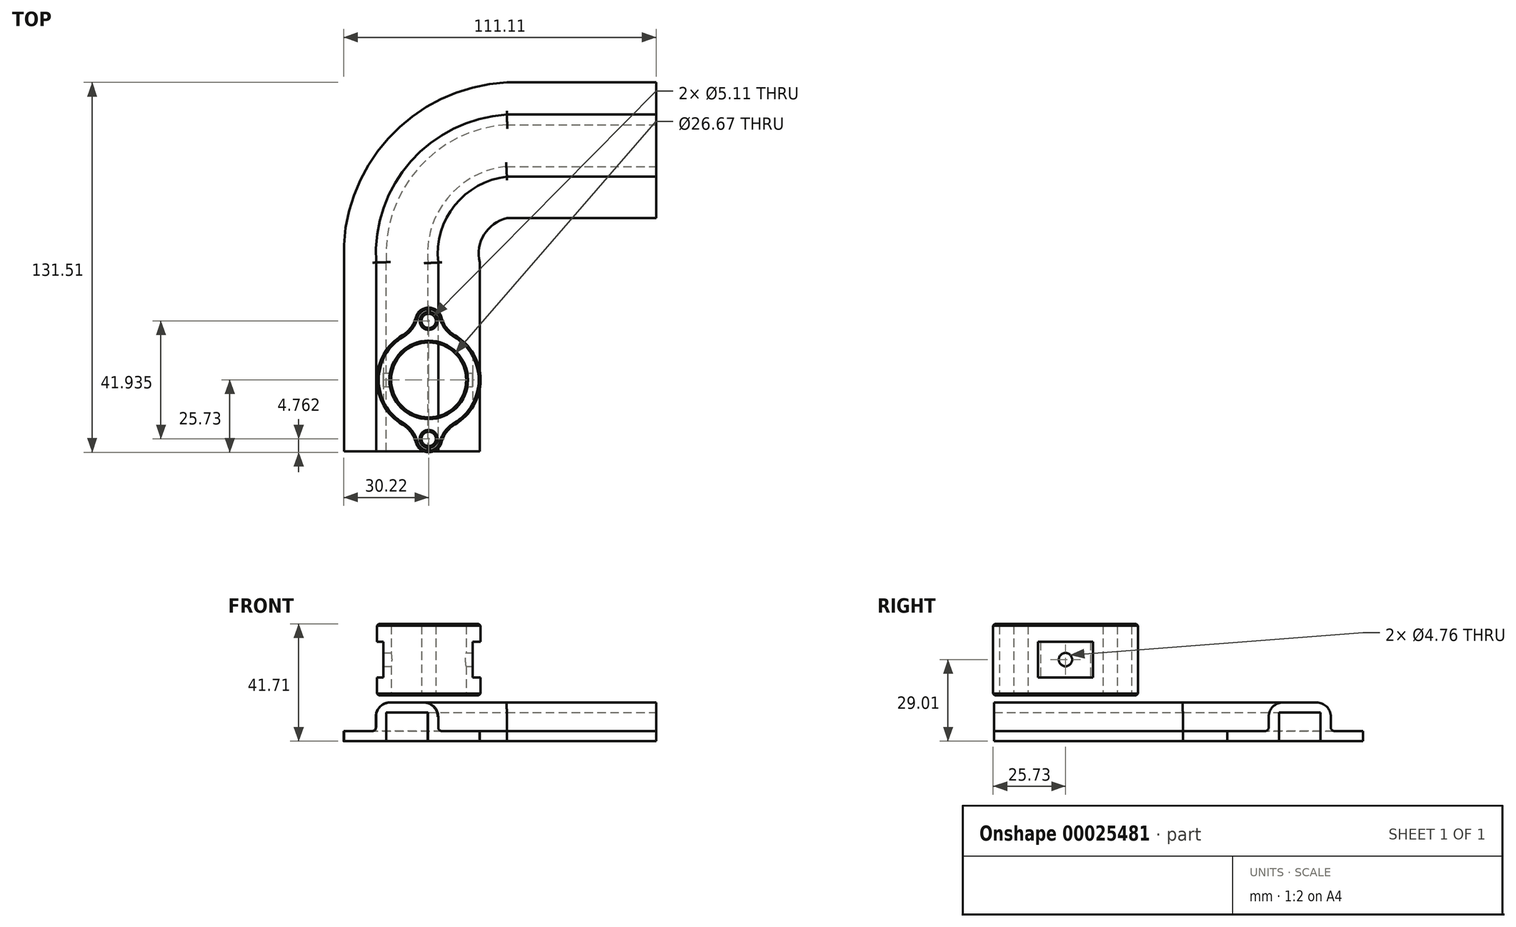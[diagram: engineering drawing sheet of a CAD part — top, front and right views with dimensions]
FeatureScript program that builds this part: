
annotation { "Feature Type Name" : "Feature", "Feature Type Description" : "" }
export const myFeature = defineFeature(function(context is Context, id is Id, definition is map)
    precondition{}
    {
        {
            var Q0;
            Q0=qCreatedBy(makeId("Top.planeOp"),FACE);
            var sketch = newSketch(context, id + "F0", { "sketchPlane" : qUnion([Q0])});
            skCircle(sketch, "E0", {"center": v(0, 0) * mm, "radius": 13.34 * mm});
            skCircle(sketch, "E1", {"center": v(0, 0) * mm, "radius": 18.41 * mm});
            skLineSegment(sketch, "E2.bottom", {"start": v(0, 18.41) * mm, "end": v(21.9, 18.41) * mm});
            skLineSegment(sketch, "E2.top", {"start": v(0, -18.41) * mm, "end": v(21.9, -18.41) * mm});
            skLineSegment(sketch, "E2.left", {"start": v(0, 18.41) * mm, "end": v(0, -18.42) * mm});
            skLineSegment(sketch, "E2.right", {"start": v(25.07, 15.24) * mm, "end": v(25.07, -15.24) * mm});
            skLineSegment(sketch, "E3", {"start": v(0, 0) * mm, "end": v(37.4, 0) * mm});
            skArc(sketch, "E4.0.startCap", {"start": v(0, -1.59) * mm, "mid": v(-1.59, 0) * mm, "end": v(0, 1.59) * mm});
            skArc(sketch, "E4.0.endCap", {"start": v(37.4, 1.59) * mm, "mid": v(39, 0) * mm, "end": v(37.4, -1.59) * mm});
            skLineSegment(sketch, "E4.0.left", {"start": v(0, 1.59) * mm, "end": v(37.4, 1.59) * mm});
            skLineSegment(sketch, "E4.0.right", {"start": v(0, -1.59) * mm, "end": v(37.4, -1.59) * mm});
            skPoint(sketch, "E5.visualSharp", {"position": v(25.07, 18.41) * mm});
            skArc(sketch, "E5.filletArc", {"start": v(25.07, 15.24) * mm, "mid": v(24.14, 17.49) * mm, "end": v(21.9, 18.41) * mm});
            skPoint(sketch, "E6.visualSharp", {"position": v(25.07, -18.41) * mm});
            skArc(sketch, "E6.filletArc", {"start": v(21.9, -18.42) * mm, "mid": v(24.14, -17.49) * mm, "end": v(25.07, -15.24) * mm});
            skCircle(sketch, "E7", {"center": v(0, 20.97) * mm, "radius": 2.55 * mm});
            skCircle(sketch, "E8", {"center": v(0, -20.97) * mm, "radius": 2.55 * mm});
            skCircle(sketch, "E9", {"center": v(0, 20.97) * mm, "radius": 4.76 * mm});
            skCircle(sketch, "E10", {"center": v(0, -20.97) * mm, "radius": 4.76 * mm});
            skCircle(sketch, "E11", {"center": v(-20.97, 0) * mm, "radius": 2.55 * mm});
            skCircle(sketch, "E12", {"center": v(-20.97, 0) * mm, "radius": 4.76 * mm});
            skPoint(sketch, "E13", {"position": v(25.07, 0) * mm});
            skSolve(sketch);
        }
        {
            var Q0;
            {var subQ5=sQuery(id+"F0.wireOp",EDGE,"E2.bottom");Q0=makeQuery(id+"F0.imprint","IMPRINT",FACE,{"disambiguationData":[TD([[makeQuery(id+"F0.imprint","IMPRINT",EDGE,{"derivedFrom":subQ5}),-1.0]])]});}
            var Q1;
            {var subQ5=sQuery(id+"F0.wireOp",EDGE,"E2.top");Q1=makeQuery(id+"F0.imprint","IMPRINT",FACE,{"disambiguationData":[TD([[makeQuery(id+"F0.imprint","IMPRINT",EDGE,{"derivedFrom":subQ5}),1.0]])]});}
            var Q2;
            {var subQ0=sQuery(id+"F0.wireOp",EDGE,"E2.left");var subQ1=sQuery(id+"F0.wireOp",EDGE,"E0");var subQ5=makeQuery(id+"F0.imprint","INTERSECT",VERTEX,{"disambiguationData":[OD(0.0)],"derivedFrom":[subQ1,subQ0]});Q2=makeQuery(id+"F0.imprint","IMPRINT",FACE,{"disambiguationData":[TD([[makeQuery(id+"F0.imprint","IMPRINT",EDGE,{"disambiguationData":[TD([[subQ5,-1.0]])],"derivedFrom":subQ1}),-1.0]])]});}
            var Q3;
            {var subQ0=sQuery(id+"F0.wireOp",EDGE,"E4.0.left");var subQ3=sQuery(id+"F0.wireOp",EDGE,"E0");var subQ4=makeQuery(id+"F0.imprint","INTERSECT",VERTEX,{"derivedFrom":[subQ3,subQ0]});Q3=makeQuery(id+"F0.imprint","IMPRINT",FACE,{"disambiguationData":[TD([[makeQuery(id+"F0.imprint","IMPRINT",EDGE,{"disambiguationData":[TD([[subQ4,-1.0]])],"derivedFrom":subQ3}),-1.0]])]});}
            var Q4;
            {var subQ3=sQuery(id+"F0.wireOp",EDGE,"E0");var subQ5=sQuery(id+"F0.wireOp",EDGE,"E2.left");var subQ6=makeQuery(id+"F0.imprint","INTERSECT",VERTEX,{"disambiguationData":[OD(1.0)],"derivedFrom":[subQ3,subQ5]});Q4=makeQuery(id+"F0.imprint","IMPRINT",FACE,{"disambiguationData":[TD([[makeQuery(id+"F0.imprint","IMPRINT",EDGE,{"disambiguationData":[TD([[subQ6,-1.0]])],"derivedFrom":subQ3}),-1.0]])]});}
            var Q5;
            {var subQ5=sQuery(id+"F0.wireOp",EDGE,"E7");Q5=makeQuery(id+"F0.imprint","IMPRINT",FACE,{"disambiguationData":[TD([[makeQuery(id+"F0.imprint","IMPRINT",EDGE,{"derivedFrom":subQ5}),-1.0]])]});}
            var Q6;
            {var subQ0=sQuery(id+"F0.wireOp",EDGE,"E9");var subQ3=sQuery(id+"F0.wireOp",EDGE,"E1");var subQ4=makeQuery(id+"F0.imprint","INTERSECT",VERTEX,{"disambiguationData":[OD(0.0)],"derivedFrom":[subQ3,subQ0]});Q6=makeQuery(id+"F0.imprint","IMPRINT",FACE,{"disambiguationData":[TD([[makeQuery(id+"F0.imprint","IMPRINT",EDGE,{"disambiguationData":[TD([[subQ4,-1.0]])],"derivedFrom":subQ0}),1.0]])]});}
            var Q7;
            {var subQ0=sQuery(id+"F0.wireOp",EDGE,"E9");var subQ3=sQuery(id+"F0.wireOp",EDGE,"E1");var subQ4=makeQuery(id+"F0.imprint","INTERSECT",VERTEX,{"disambiguationData":[OD(1.0)],"derivedFrom":[subQ3,subQ0]});Q7=makeQuery(id+"F0.imprint","IMPRINT",FACE,{"disambiguationData":[TD([[makeQuery(id+"F0.imprint","IMPRINT",EDGE,{"disambiguationData":[TD([[subQ4,1.0]])],"derivedFrom":subQ0}),1.0]])]});}
            var Q8;
            {var subQ5=sQuery(id+"F0.wireOp",EDGE,"E8");Q8=makeQuery(id+"F0.imprint","IMPRINT",FACE,{"disambiguationData":[TD([[makeQuery(id+"F0.imprint","IMPRINT",EDGE,{"derivedFrom":subQ5}),-1.0]])]});}
            var Q9;
            {var subQ0=sQuery(id+"F0.wireOp",EDGE,"E10");var subQ3=sQuery(id+"F0.wireOp",EDGE,"E1");var subQ4=makeQuery(id+"F0.imprint","INTERSECT",VERTEX,{"disambiguationData":[OD(0.0)],"derivedFrom":[subQ3,subQ0]});Q9=makeQuery(id+"F0.imprint","IMPRINT",FACE,{"disambiguationData":[TD([[makeQuery(id+"F0.imprint","IMPRINT",EDGE,{"disambiguationData":[TD([[subQ4,1.0]])],"derivedFrom":subQ0}),1.0]])]});}
            var Q10;
            {var subQ0=sQuery(id+"F0.wireOp",EDGE,"E10");var subQ3=sQuery(id+"F0.wireOp",EDGE,"E1");var subQ4=makeQuery(id+"F0.imprint","INTERSECT",VERTEX,{"disambiguationData":[OD(1.0)],"derivedFrom":[subQ3,subQ0]});Q10=makeQuery(id+"F0.imprint","IMPRINT",FACE,{"disambiguationData":[TD([[makeQuery(id+"F0.imprint","IMPRINT",EDGE,{"disambiguationData":[TD([[subQ4,-1.0]])],"derivedFrom":subQ0}),1.0]])]});}
            var Q11;
            {var subQ0=sQuery(id+"F0.wireOp",EDGE,"E12");var subQ1=sQuery(id+"F0.wireOp",EDGE,"E1");var subQ3=makeQuery(id+"F0.imprint","INTERSECT",VERTEX,{"disambiguationData":[OD(0.0)],"derivedFrom":[subQ1,subQ0]});Q11=makeQuery(id+"F0.imprint","IMPRINT",FACE,{"disambiguationData":[TD([[makeQuery(id+"F0.imprint","IMPRINT",EDGE,{"disambiguationData":[TD([[subQ3,-1.0]])],"derivedFrom":subQ1}),1.0]])]});}
            var Q12;
            {var subQ3=sQuery(id+"F0.wireOp",EDGE,"E0");var subQ5=sQuery(id+"F0.wireOp",EDGE,"E4.0.left");var subQ7=makeQuery(id+"F0.imprint","INTERSECT",VERTEX,{"derivedFrom":[subQ3,subQ5]});Q12=makeQuery(id+"F0.imprint","IMPRINT",FACE,{"disambiguationData":[TD([[makeQuery(id+"F0.imprint","IMPRINT",EDGE,{"disambiguationData":[TD([[subQ7,1.0]])],"derivedFrom":subQ3}),-1.0]])]});}
            var Q13;
            {var subQ3=sQuery(id+"F0.wireOp",EDGE,"E0");var subQ5=sQuery(id+"F0.wireOp",EDGE,"E3");var subQ7=makeQuery(id+"F0.imprint","INTERSECT",VERTEX,{"derivedFrom":[subQ3,subQ5]});Q13=makeQuery(id+"F0.imprint","IMPRINT",FACE,{"disambiguationData":[TD([[makeQuery(id+"F0.imprint","IMPRINT",EDGE,{"disambiguationData":[TD([[subQ7,1.0]])],"derivedFrom":subQ3}),-1.0]])]});}
            extrude(context, id + "F1", {"entities" : qUnion([Q0, Q1, Q2, Q3, Q4, Q5, Q6, Q7, Q8, Q9, Q10, Q11, Q12, Q13]), "depth" : 25.4 * mm});
        }
        {
            var Q0;
            Q0=makeQuery(id+"F1.opExtrude","SWEPT_EDGE",EDGE,{"disambiguationData":[OSD([sQuery(id+"F0.wireOp",EDGE,"E2.bottom"),sQuery(id+"F0.wireOp",EDGE,"E9")])]});
            var Q1;
            Q1=makeQuery(id+"F1.opExtrude","SWEPT_EDGE",EDGE,{"disambiguationData":[OSD([sQuery(id+"F0.wireOp",EDGE,"E1"),sQuery(id+"F0.wireOp",EDGE,"E9")])]});
            var Q2;
            Q2=makeQuery(id+"F1.opExtrude","SWEPT_EDGE",EDGE,{"disambiguationData":[OSD([sQuery(id+"F0.wireOp",EDGE,"E2.top"),sQuery(id+"F0.wireOp",EDGE,"E10")])]});
            var Q3;
            Q3=makeQuery(id+"F1.opExtrude","SWEPT_EDGE",EDGE,{"disambiguationData":[OSD([sQuery(id+"F0.wireOp",EDGE,"E1"),sQuery(id+"F0.wireOp",EDGE,"E10")])]});
            var Q4;
            {var subQ0=sQuery(id+"F0.wireOp",EDGE,"E1");var subQ1=sQuery(id+"F0.wireOp",EDGE,"E12");Q4=makeQuery(id+"F1.opExtrude","SWEPT_EDGE",EDGE,{"disambiguationData":[OSD([subQ0,subQ1]),TDD([makeQuery(id+"F0.imprint","INTERSECT",VERTEX,{"disambiguationData":[OD(1.0)],"derivedFrom":[subQ0,subQ1]})])]});}
            var Q5;
            {var subQ0=sQuery(id+"F0.wireOp",EDGE,"E1");var subQ1=sQuery(id+"F0.wireOp",EDGE,"E12");Q5=makeQuery(id+"F1.opExtrude","SWEPT_EDGE",EDGE,{"disambiguationData":[OSD([subQ0,subQ1]),TDD([makeQuery(id+"F0.imprint","INTERSECT",VERTEX,{"disambiguationData":[OD(0.0)],"derivedFrom":[subQ0,subQ1]})])]});}
            fillet(context, id + "F2", {"entities" : qUnion([Q0, Q1, Q2, Q3, Q4, Q5]), "radius" : 10.16 * mm, "tangentPropagation" : true, "allowEdgeOverflow" : false});
        }
        {
            var Q0;
            {var subQ0=sQuery(id+"F0.wireOp",EDGE,"E2.right");Q0=makeQuery(id+"F1.opExtrude","CAP_EDGE",EDGE,{"disambiguationData":[OSD([subQ0]),TDD([makeQuery(id+"F0.imprint","IMPRINT",EDGE,{"disambiguationData":[TD([[makeQuery(id+"F0.imprint","INTERSECT",VERTEX,{"derivedFrom":[subQ0,sQuery(id+"F0.wireOp",EDGE,"E6.filletArc")]}),1.0]])],"derivedFrom":subQ0})])],"isStart":false});}
            var Q1;
            Q1=makeQuery(id+"F1.opExtrude","CAP_EDGE",EDGE,{"disambiguationData":[OSD([sQuery(id+"F0.wireOp",EDGE,"E6.filletArc")])],"isStart":false});
            var Q2;
            Q2=makeQuery(id+"F1.opExtrude","CAP_EDGE",EDGE,{"disambiguationData":[OSD([sQuery(id+"F0.wireOp",EDGE,"E2.top")])],"isStart":false});
            var Q3;
            {var subQ0=sQuery(id+"F0.wireOp",EDGE,"E2.top");var subQ1=sQuery(id+"F0.wireOp",EDGE,"E10");Q3=makeQuery(id+"F2.opFillet","BLEND_EDGE",EDGE,{"blendedFrom":[makeQuery(id+"F1.opExtrude","SWEPT_EDGE",EDGE,{"disambiguationData":[OSD([subQ0,subQ1])]}),makeQuery(id+"F1.opExtrude","CAP_FACE",FACE,{"disambiguationData":[OSD([sQuery(id+"F0.wireOp",EDGE,"E0"),sQuery(id+"F0.wireOp",EDGE,"E1"),sQuery(id+"F0.wireOp",EDGE,"E2.bottom"),subQ0,sQuery(id+"F0.wireOp",EDGE,"E2.right"),sQuery(id+"F0.wireOp",EDGE,"E4.0.left"),sQuery(id+"F0.wireOp",EDGE,"E4.0.right"),sQuery(id+"F0.wireOp",EDGE,"E5.filletArc"),sQuery(id+"F0.wireOp",EDGE,"E6.filletArc"),sQuery(id+"F0.wireOp",EDGE,"E7"),sQuery(id+"F0.wireOp",EDGE,"E8"),sQuery(id+"F0.wireOp",EDGE,"E9"),subQ1])],"isStart":false})],"blendedInto":[makeQuery(id+"F1.opExtrude","CAP_FACE",FACE,{"disambiguationData":[OSD([sQuery(id+"F0.wireOp",EDGE,"E0"),sQuery(id+"F0.wireOp",EDGE,"E1"),sQuery(id+"F0.wireOp",EDGE,"E2.bottom"),subQ0,sQuery(id+"F0.wireOp",EDGE,"E2.right"),sQuery(id+"F0.wireOp",EDGE,"E4.0.left"),sQuery(id+"F0.wireOp",EDGE,"E4.0.right"),sQuery(id+"F0.wireOp",EDGE,"E5.filletArc"),sQuery(id+"F0.wireOp",EDGE,"E6.filletArc"),sQuery(id+"F0.wireOp",EDGE,"E7"),sQuery(id+"F0.wireOp",EDGE,"E8"),sQuery(id+"F0.wireOp",EDGE,"E9"),subQ1])],"isStart":false})]});}
            var Q4;
            Q4=makeQuery(id+"F1.opExtrude","CAP_EDGE",EDGE,{"disambiguationData":[OSD([sQuery(id+"F0.wireOp",EDGE,"E10")])],"isStart":false});
            var Q5;
            {var subQ0=sQuery(id+"F0.wireOp",EDGE,"E1");var subQ1=sQuery(id+"F0.wireOp",EDGE,"E10");Q5=makeQuery(id+"F2.opFillet","BLEND_EDGE",EDGE,{"blendedFrom":[makeQuery(id+"F1.opExtrude","SWEPT_EDGE",EDGE,{"disambiguationData":[OSD([subQ0,subQ1])]}),makeQuery(id+"F1.opExtrude","CAP_FACE",FACE,{"disambiguationData":[OSD([sQuery(id+"F0.wireOp",EDGE,"E0"),subQ0,sQuery(id+"F0.wireOp",EDGE,"E2.bottom"),sQuery(id+"F0.wireOp",EDGE,"E2.top"),sQuery(id+"F0.wireOp",EDGE,"E2.right"),sQuery(id+"F0.wireOp",EDGE,"E4.0.left"),sQuery(id+"F0.wireOp",EDGE,"E4.0.right"),sQuery(id+"F0.wireOp",EDGE,"E5.filletArc"),sQuery(id+"F0.wireOp",EDGE,"E6.filletArc"),sQuery(id+"F0.wireOp",EDGE,"E7"),sQuery(id+"F0.wireOp",EDGE,"E8"),sQuery(id+"F0.wireOp",EDGE,"E9"),subQ1])],"isStart":false})],"blendedInto":[makeQuery(id+"F1.opExtrude","CAP_FACE",FACE,{"disambiguationData":[OSD([sQuery(id+"F0.wireOp",EDGE,"E0"),subQ0,sQuery(id+"F0.wireOp",EDGE,"E2.bottom"),sQuery(id+"F0.wireOp",EDGE,"E2.top"),sQuery(id+"F0.wireOp",EDGE,"E2.right"),sQuery(id+"F0.wireOp",EDGE,"E4.0.left"),sQuery(id+"F0.wireOp",EDGE,"E4.0.right"),sQuery(id+"F0.wireOp",EDGE,"E5.filletArc"),sQuery(id+"F0.wireOp",EDGE,"E6.filletArc"),sQuery(id+"F0.wireOp",EDGE,"E7"),sQuery(id+"F0.wireOp",EDGE,"E8"),sQuery(id+"F0.wireOp",EDGE,"E9"),subQ1])],"isStart":false})]});}
            var Q6;
            Q6=makeQuery(id+"F1.opExtrude","CAP_EDGE",EDGE,{"disambiguationData":[OSD([sQuery(id+"F0.wireOp",EDGE,"E1")])],"isStart":false});
            var Q7;
            {var subQ0=sQuery(id+"F0.wireOp",EDGE,"E1");var subQ1=sQuery(id+"F0.wireOp",EDGE,"E9");Q7=makeQuery(id+"F2.opFillet","BLEND_EDGE",EDGE,{"blendedFrom":[makeQuery(id+"F1.opExtrude","SWEPT_EDGE",EDGE,{"disambiguationData":[OSD([subQ0,subQ1])]}),makeQuery(id+"F1.opExtrude","CAP_FACE",FACE,{"disambiguationData":[OSD([sQuery(id+"F0.wireOp",EDGE,"E0"),subQ0,sQuery(id+"F0.wireOp",EDGE,"E2.bottom"),sQuery(id+"F0.wireOp",EDGE,"E2.top"),sQuery(id+"F0.wireOp",EDGE,"E2.right"),sQuery(id+"F0.wireOp",EDGE,"E4.0.left"),sQuery(id+"F0.wireOp",EDGE,"E4.0.right"),sQuery(id+"F0.wireOp",EDGE,"E5.filletArc"),sQuery(id+"F0.wireOp",EDGE,"E6.filletArc"),sQuery(id+"F0.wireOp",EDGE,"E7"),sQuery(id+"F0.wireOp",EDGE,"E8"),subQ1,sQuery(id+"F0.wireOp",EDGE,"E10")])],"isStart":false})],"blendedInto":[makeQuery(id+"F1.opExtrude","CAP_FACE",FACE,{"disambiguationData":[OSD([sQuery(id+"F0.wireOp",EDGE,"E0"),subQ0,sQuery(id+"F0.wireOp",EDGE,"E2.bottom"),sQuery(id+"F0.wireOp",EDGE,"E2.top"),sQuery(id+"F0.wireOp",EDGE,"E2.right"),sQuery(id+"F0.wireOp",EDGE,"E4.0.left"),sQuery(id+"F0.wireOp",EDGE,"E4.0.right"),sQuery(id+"F0.wireOp",EDGE,"E5.filletArc"),sQuery(id+"F0.wireOp",EDGE,"E6.filletArc"),sQuery(id+"F0.wireOp",EDGE,"E7"),sQuery(id+"F0.wireOp",EDGE,"E8"),subQ1,sQuery(id+"F0.wireOp",EDGE,"E10")])],"isStart":false})]});}
            var Q8;
            Q8=makeQuery(id+"F1.opExtrude","CAP_EDGE",EDGE,{"disambiguationData":[OSD([sQuery(id+"F0.wireOp",EDGE,"E9")])],"isStart":false});
            var Q9;
            {var subQ0=sQuery(id+"F0.wireOp",EDGE,"E2.bottom");var subQ1=sQuery(id+"F0.wireOp",EDGE,"E9");Q9=makeQuery(id+"F2.opFillet","BLEND_EDGE",EDGE,{"blendedFrom":[makeQuery(id+"F1.opExtrude","SWEPT_EDGE",EDGE,{"disambiguationData":[OSD([subQ0,subQ1])]}),makeQuery(id+"F1.opExtrude","CAP_FACE",FACE,{"disambiguationData":[OSD([sQuery(id+"F0.wireOp",EDGE,"E0"),sQuery(id+"F0.wireOp",EDGE,"E1"),subQ0,sQuery(id+"F0.wireOp",EDGE,"E2.top"),sQuery(id+"F0.wireOp",EDGE,"E2.right"),sQuery(id+"F0.wireOp",EDGE,"E4.0.left"),sQuery(id+"F0.wireOp",EDGE,"E4.0.right"),sQuery(id+"F0.wireOp",EDGE,"E5.filletArc"),sQuery(id+"F0.wireOp",EDGE,"E6.filletArc"),sQuery(id+"F0.wireOp",EDGE,"E7"),sQuery(id+"F0.wireOp",EDGE,"E8"),subQ1,sQuery(id+"F0.wireOp",EDGE,"E10")])],"isStart":false})],"blendedInto":[makeQuery(id+"F1.opExtrude","CAP_FACE",FACE,{"disambiguationData":[OSD([sQuery(id+"F0.wireOp",EDGE,"E0"),sQuery(id+"F0.wireOp",EDGE,"E1"),subQ0,sQuery(id+"F0.wireOp",EDGE,"E2.top"),sQuery(id+"F0.wireOp",EDGE,"E2.right"),sQuery(id+"F0.wireOp",EDGE,"E4.0.left"),sQuery(id+"F0.wireOp",EDGE,"E4.0.right"),sQuery(id+"F0.wireOp",EDGE,"E5.filletArc"),sQuery(id+"F0.wireOp",EDGE,"E6.filletArc"),sQuery(id+"F0.wireOp",EDGE,"E7"),sQuery(id+"F0.wireOp",EDGE,"E8"),subQ1,sQuery(id+"F0.wireOp",EDGE,"E10")])],"isStart":false})]});}
            var Q10;
            Q10=makeQuery(id+"F1.opExtrude","CAP_EDGE",EDGE,{"disambiguationData":[OSD([sQuery(id+"F0.wireOp",EDGE,"E2.bottom")])],"isStart":false});
            var Q11;
            Q11=makeQuery(id+"F1.opExtrude","CAP_EDGE",EDGE,{"disambiguationData":[OSD([sQuery(id+"F0.wireOp",EDGE,"E5.filletArc")])],"isStart":false});
            var Q12;
            {var subQ0=sQuery(id+"F0.wireOp",EDGE,"E2.right");Q12=makeQuery(id+"F1.opExtrude","CAP_EDGE",EDGE,{"disambiguationData":[OSD([subQ0]),TDD([makeQuery(id+"F0.imprint","IMPRINT",EDGE,{"disambiguationData":[TD([[makeQuery(id+"F0.imprint","INTERSECT",VERTEX,{"derivedFrom":[subQ0,sQuery(id+"F0.wireOp",EDGE,"E5.filletArc")]}),-1.0]])],"derivedFrom":subQ0})])],"isStart":false});}
            var Q13;
            Q13=makeQuery(id+"F1.opExtrude","CAP_EDGE",EDGE,{"disambiguationData":[OSD([sQuery(id+"F0.wireOp",EDGE,"E0")])],"isStart":false});
            var Q14;
            {var subQ0=sQuery(id+"F0.wireOp",EDGE,"E2.right");Q14=makeQuery(id+"F1.opExtrude","CAP_EDGE",EDGE,{"disambiguationData":[OSD([subQ0]),TDD([makeQuery(id+"F0.imprint","IMPRINT",EDGE,{"disambiguationData":[TD([[makeQuery(id+"F0.imprint","INTERSECT",VERTEX,{"derivedFrom":[subQ0,sQuery(id+"F0.wireOp",EDGE,"E6.filletArc")]}),1.0]])],"derivedFrom":subQ0})])],"isStart":true});}
            var Q15;
            Q15=makeQuery(id+"F1.opExtrude","CAP_EDGE",EDGE,{"disambiguationData":[OSD([sQuery(id+"F0.wireOp",EDGE,"E6.filletArc")])],"isStart":true});
            var Q16;
            {var subQ0=sQuery(id+"F0.wireOp",EDGE,"E1");var subQ1=sQuery(id+"F0.wireOp",EDGE,"E10");Q16=makeQuery(id+"F2.opFillet","BLEND_EDGE",EDGE,{"blendedFrom":[makeQuery(id+"F1.opExtrude","SWEPT_EDGE",EDGE,{"disambiguationData":[OSD([subQ0,subQ1]),TDD([makeQuery(id+"F0.imprint","INTERSECT",VERTEX,{"disambiguationData":[OD(1.0)],"derivedFrom":[subQ0,subQ1]})])]}),makeQuery(id+"F1.opExtrude","CAP_FACE",FACE,{"disambiguationData":[OSD([sQuery(id+"F0.wireOp",EDGE,"E0"),subQ0,sQuery(id+"F0.wireOp",EDGE,"E7"),sQuery(id+"F0.wireOp",EDGE,"E8"),sQuery(id+"F0.wireOp",EDGE,"E9"),subQ1])],"isStart":true})],"blendedInto":[makeQuery(id+"F1.opExtrude","CAP_FACE",FACE,{"disambiguationData":[OSD([sQuery(id+"F0.wireOp",EDGE,"E0"),subQ0,sQuery(id+"F0.wireOp",EDGE,"E7"),sQuery(id+"F0.wireOp",EDGE,"E8"),sQuery(id+"F0.wireOp",EDGE,"E9"),subQ1])],"isStart":true})]});}
            var Q17;
            Q17=makeQuery(id+"F1.opExtrude","CAP_EDGE",EDGE,{"disambiguationData":[OSD([sQuery(id+"F0.wireOp",EDGE,"E0")])],"isStart":true});
            var Q18;
            Q18=makeQuery(id+"F1.opExtrude","CAP_EDGE",EDGE,{"disambiguationData":[OSD([sQuery(id+"F0.wireOp",EDGE,"E8")])],"isStart":false});
            var Q19;
            Q19=makeQuery(id+"F1.opExtrude","CAP_EDGE",EDGE,{"disambiguationData":[OSD([sQuery(id+"F0.wireOp",EDGE,"E7")])],"isStart":false});
            var Q20;
            Q20=makeQuery(id+"F1.opExtrude","CAP_EDGE",EDGE,{"disambiguationData":[OSD([sQuery(id+"F0.wireOp",EDGE,"E8")])],"isStart":true});
            var Q21;
            Q21=makeQuery(id+"F1.opExtrude","CAP_EDGE",EDGE,{"disambiguationData":[OSD([sQuery(id+"F0.wireOp",EDGE,"E7")])],"isStart":true});
            chamfer(context, id + "F3", {"entities" : qUnion([Q0, Q1, Q2, Q3, Q4, Q5, Q6, Q7, Q8, Q9, Q10, Q11, Q12, Q13, Q14, Q15, Q16, Q17, Q18, Q19, Q20, Q21]), "width" : 0.64 * mm, "tangentPropagation" : true});
        }
        {
            var Q0;
            Q0=qCreatedBy(makeId("Front.planeOp"),FACE);
            var sketch = newSketch(context, id + "F4", { "sketchPlane" : qUnion([Q0])});
            skLineSegment(sketch, "E14", {"start": v(-30.14, -12.68) * mm, "end": v(-18.71, -12.68) * mm});
            skLineSegment(sketch, "E15", {"start": v(-18.71, -12.68) * mm, "end": v(-18.71, -2.52) * mm});
            skLineSegment(sketch, "E16", {"start": v(-18.71, -2.52) * mm, "end": v(3.39, -2.52) * mm});
            skLineSegment(sketch, "E17", {"start": v(3.39, -2.52) * mm, "end": v(3.39, -12.68) * mm});
            skLineSegment(sketch, "E18", {"start": v(3.39, -12.68) * mm, "end": v(18.12, -12.68) * mm});
            skLineSegment(sketch, "E19.0", {"start": v(-0.25, -16.3) * mm, "end": v(18.12, -16.3) * mm});
            skLineSegment(sketch, "E19.1", {"start": v(-30.14, -16.3) * mm, "end": v(-15.08, -16.3) * mm});
            skLineSegment(sketch, "E19.2", {"start": v(-15.08, -16.3) * mm, "end": v(-15.08, -6.15) * mm});
            skLineSegment(sketch, "E19.3", {"start": v(-15.08, -6.15) * mm, "end": v(-0.25, -6.15) * mm});
            skLineSegment(sketch, "E19.4", {"start": v(-0.25, -6.15) * mm, "end": v(-0.25, -16.3) * mm});
            skLineSegment(sketch, "E20", {"start": v(-30.14, -16.3) * mm, "end": v(-30.14, -12.68) * mm});
            skLineSegment(sketch, "E21", {"start": v(18.12, -16.3) * mm, "end": v(18.12, -12.68) * mm});
            skSolve(sketch);
        }
        {
            var Q0;
            Q0 = qSketchRegion(id + "F4", true);
            extrude(context, id + "F5", {"entities" : qUnion([Q0]), "depth" : 25.4 * mm});
        }
        {
            var Q0;
            Q0=qCreatedBy(makeId("Top.planeOp"),FACE);
            var sketch = newSketch(context, id + "F6", { "sketchPlane" : qUnion([Q0])});
            skLineSegment(sketch, "E22", {"start": v(-7.25, 3.05) * mm, "end": v(-7.25, 44.79) * mm});
            skLineSegment(sketch, "E23", {"start": v(30.85, 82.89) * mm, "end": v(83.94, 82.89) * mm});
            skPoint(sketch, "E24.visualSharp", {"position": v(-7.25, 82.89) * mm});
            skArc(sketch, "E24.filletArc", {"start": v(30.85, 82.89) * mm, "mid": v(3.91, 71.73) * mm, "end": v(-7.25, 44.79) * mm});
            skSolve(sketch);
        }
        {
            var Q0;
            Q0=makeQuery(id+"F5.opExtrude","CAP_FACE",FACE,{"disambiguationData":[OSD([sQuery(id+"F4.wireOp",EDGE,"E14"),sQuery(id+"F4.wireOp",EDGE,"E15"),sQuery(id+"F4.wireOp",EDGE,"E16"),sQuery(id+"F4.wireOp",EDGE,"E17"),sQuery(id+"F4.wireOp",EDGE,"E18"),sQuery(id+"F4.wireOp",EDGE,"E19.0"),sQuery(id+"F4.wireOp",EDGE,"E19.1"),sQuery(id+"F4.wireOp",EDGE,"E19.2"),sQuery(id+"F4.wireOp",EDGE,"E19.3"),sQuery(id+"F4.wireOp",EDGE,"E19.4"),sQuery(id+"F4.wireOp",EDGE,"E20"),sQuery(id+"F4.wireOp",EDGE,"E21")])],"isStart":true});
            var Q1;
            Q1=sQuery(id+"F6.wireOp",EDGE,"E22");
            var Q2;
            Q2=sQuery(id+"F6.wireOp",EDGE,"E24.filletArc");
            var Q3;
            Q3=sQuery(id+"F6.wireOp",EDGE,"E23");
            sweep(context, id + "F7", {"operationType" : NewBodyOperationType.ADD, "profiles" : qUnion([Q0]), "path" : qUnion([Q1, Q2, Q3])});
        }
        {
            var Q0;
            Q0=makeQuery(id+"F7.opSweep","SWEPT_EDGE",EDGE,{"disambiguationData":[OSD([sQuery(id+"F4.wireOp",EDGE,"E16"),sQuery(id+"F4.wireOp",EDGE,"E17"),sQuery(id+"F6.wireOp",EDGE,"E23")])]});
            var Q1;
            Q1=makeQuery(id+"F7.opSweep","SWEPT_EDGE",EDGE,{"disambiguationData":[OSD([sQuery(id+"F4.wireOp",EDGE,"E16"),sQuery(id+"F4.wireOp",EDGE,"E17"),sQuery(id+"F6.wireOp",EDGE,"E24.filletArc")])]});
            var Q2;
            {var subQ0=sQuery(id+"F4.wireOp",EDGE,"E16");var subQ1=sQuery(id+"F4.wireOp",EDGE,"E17");Q2=makeQuery(id+"F7.boolean.opBoolean","MERGE",EDGE,{"derivedFrom":[makeQuery(id+"F5.opExtrude","SWEPT_EDGE",EDGE,{"disambiguationData":[OSD([subQ0,subQ1])]}),makeQuery(id+"F7.opSweep","SWEPT_EDGE",EDGE,{"disambiguationData":[OSD([subQ0,subQ1,sQuery(id+"F6.wireOp",EDGE,"E22")])]})]});}
            var Q3;
            {var subQ0=sQuery(id+"F4.wireOp",EDGE,"E15");var subQ1=sQuery(id+"F4.wireOp",EDGE,"E16");Q3=makeQuery(id+"F7.boolean.opBoolean","MERGE",EDGE,{"derivedFrom":[makeQuery(id+"F5.opExtrude","SWEPT_EDGE",EDGE,{"disambiguationData":[OSD([subQ0,subQ1])]}),makeQuery(id+"F7.opSweep","SWEPT_EDGE",EDGE,{"disambiguationData":[OSD([subQ0,subQ1,sQuery(id+"F6.wireOp",EDGE,"E22")])]})]});}
            var Q4;
            Q4=makeQuery(id+"F7.opSweep","SWEPT_EDGE",EDGE,{"disambiguationData":[OSD([sQuery(id+"F4.wireOp",EDGE,"E15"),sQuery(id+"F4.wireOp",EDGE,"E16"),sQuery(id+"F6.wireOp",EDGE,"E24.filletArc")])]});
            var Q5;
            Q5=makeQuery(id+"F7.opSweep","SWEPT_EDGE",EDGE,{"disambiguationData":[OSD([sQuery(id+"F4.wireOp",EDGE,"E15"),sQuery(id+"F4.wireOp",EDGE,"E16"),sQuery(id+"F6.wireOp",EDGE,"E23")])]});
            fillet(context, id + "F8", {"entities" : qUnion([Q0, Q1, Q2, Q3, Q4, Q5]), "radius" : 5.08 * mm, "tangentPropagation" : true, "allowEdgeOverflow" : false});
        }
        {
            var Q0;
            Q0=makeQuery(id+"F7.opSweep","SWEPT_EDGE",EDGE,{"disambiguationData":[OSD([sQuery(id+"F4.wireOp",EDGE,"E14"),sQuery(id+"F4.wireOp",EDGE,"E15"),sQuery(id+"F6.wireOp",EDGE,"E23")])]});
            var Q1;
            Q1=makeQuery(id+"F7.opSweep","SWEPT_EDGE",EDGE,{"disambiguationData":[OSD([sQuery(id+"F4.wireOp",EDGE,"E14"),sQuery(id+"F4.wireOp",EDGE,"E15"),sQuery(id+"F6.wireOp",EDGE,"E24.filletArc")])]});
            var Q2;
            {var subQ0=sQuery(id+"F4.wireOp",EDGE,"E14");var subQ1=sQuery(id+"F4.wireOp",EDGE,"E15");Q2=makeQuery(id+"F7.boolean.opBoolean","MERGE",EDGE,{"derivedFrom":[makeQuery(id+"F5.opExtrude","SWEPT_EDGE",EDGE,{"disambiguationData":[OSD([subQ0,subQ1])]}),makeQuery(id+"F7.opSweep","SWEPT_EDGE",EDGE,{"disambiguationData":[OSD([subQ0,subQ1,sQuery(id+"F6.wireOp",EDGE,"E22")])]})]});}
            var Q3;
            {var subQ0=sQuery(id+"F4.wireOp",EDGE,"E17");var subQ1=sQuery(id+"F4.wireOp",EDGE,"E18");Q3=makeQuery(id+"F7.boolean.opBoolean","MERGE",EDGE,{"derivedFrom":[makeQuery(id+"F5.opExtrude","SWEPT_EDGE",EDGE,{"disambiguationData":[OSD([subQ0,subQ1])]}),makeQuery(id+"F7.opSweep","SWEPT_EDGE",EDGE,{"disambiguationData":[OSD([subQ0,subQ1,sQuery(id+"F6.wireOp",EDGE,"E22")])]})]});}
            var Q4;
            Q4=makeQuery(id+"F7.opSweep","SWEPT_EDGE",EDGE,{"disambiguationData":[OSD([sQuery(id+"F4.wireOp",EDGE,"E17"),sQuery(id+"F4.wireOp",EDGE,"E18"),sQuery(id+"F6.wireOp",EDGE,"E24.filletArc")])]});
            var Q5;
            Q5=makeQuery(id+"F7.opSweep","SWEPT_EDGE",EDGE,{"disambiguationData":[OSD([sQuery(id+"F4.wireOp",EDGE,"E17"),sQuery(id+"F4.wireOp",EDGE,"E18"),sQuery(id+"F6.wireOp",EDGE,"E23")])]});
            fillet(context, id + "F9", {"entities" : qUnion([Q0, Q1, Q2, Q3, Q4, Q5]), "radius" : 1.27 * mm, "tangentPropagation" : true, "allowEdgeOverflow" : false});
        }
        {
            var Q0;
            Q0=qCreatedBy(makeId("Front.planeOp"),FACE);
            var sketch = newSketch(context, id + "F10", { "sketchPlane" : qUnion([Q0])});
            skLineSegment(sketch, "E25", {"start": v(-22.48, 12.7) * mm, "end": v(21.97, 12.7) * mm, "construction": true});
            skLineSegment(sketch, "E26.rect.bottom", {"start": v(-16.13, 6.35) * mm, "end": v(-28.83, 6.35) * mm});
            skLineSegment(sketch, "E26.rect.top", {"start": v(-16.13, 19.05) * mm, "end": v(-28.83, 19.05) * mm});
            skLineSegment(sketch, "E26.rect.left", {"start": v(-16.13, 6.35) * mm, "end": v(-16.13, 19.05) * mm});
            skLineSegment(sketch, "E26.rect.right", {"start": v(-28.83, 6.35) * mm, "end": v(-28.83, 19.05) * mm});
            skPoint(sketch, "E26.rect.middle", {"position": v(-22.48, 12.7) * mm});
            skLineSegment(sketch, "E27.rect.bottom", {"start": v(15.62, 6.35) * mm, "end": v(28.32, 6.35) * mm});
            skLineSegment(sketch, "E27.rect.top", {"start": v(15.62, 19.05) * mm, "end": v(28.32, 19.05) * mm});
            skLineSegment(sketch, "E27.rect.left", {"start": v(15.62, 6.35) * mm, "end": v(15.62, 19.05) * mm});
            skLineSegment(sketch, "E27.rect.right", {"start": v(28.32, 6.35) * mm, "end": v(28.32, 19.05) * mm});
            skPoint(sketch, "E27.rect.middle", {"position": v(21.97, 12.7) * mm});
            skLineSegment(sketch, "E28", {"start": v(-0.25, -8.13) * mm, "end": v(-0.25, 32.12) * mm, "construction": true});
            skPoint(sketch, "E28.startSnap0", {"position": v(-0.25, 12.7) * mm});
            skSolve(sketch);
        }
        {
            var Q0;
            Q0 = qSketchRegion(id + "F10", true);
            extrude(context, id + "F11", {"entities" : qUnion([Q0]), "operationType" : NewBodyOperationType.REMOVE, "endBound" : BoundingType.SYMMETRIC, "oppositeDirection" : true, "depth" : 51.8 * mm});
        }
        {
            var Q0;
            Q0=makeQuery(id+"F11.boolean.opBoolean","COPY",FACE,{"derivedFrom":makeQuery(id+"F11.opExtrude","SWEPT_FACE",FACE,{"disambiguationData":[OSD([sQuery(id+"F10.wireOp",EDGE,"E27.rect.left")])]})});
            var sketch = newSketch(context, id + "F12", { "sketchPlane" : qUnion([Q0])});
            skCircle(sketch, "E29", {"center": v(0, 12.7) * mm, "radius": 2.38 * mm});
            skPoint(sketch, "E29.centerSnap0", {"position": v(0, 19.05) * mm});
            skPoint(sketch, "E29.centerSnap1", {"position": v(-9.75, 12.7) * mm});
            skSolve(sketch);
        }
        {
            var Q0;
            Q0 = qSketchRegion(id + "F12", true);
            extrude(context, id + "F13", {"entities" : qUnion([Q0]), "operationType" : NewBodyOperationType.REMOVE, "endBound" : BoundingType.THROUGH_ALL, "oppositeDirection" : true, "depth" : 25.4 * mm});
        }
    });
